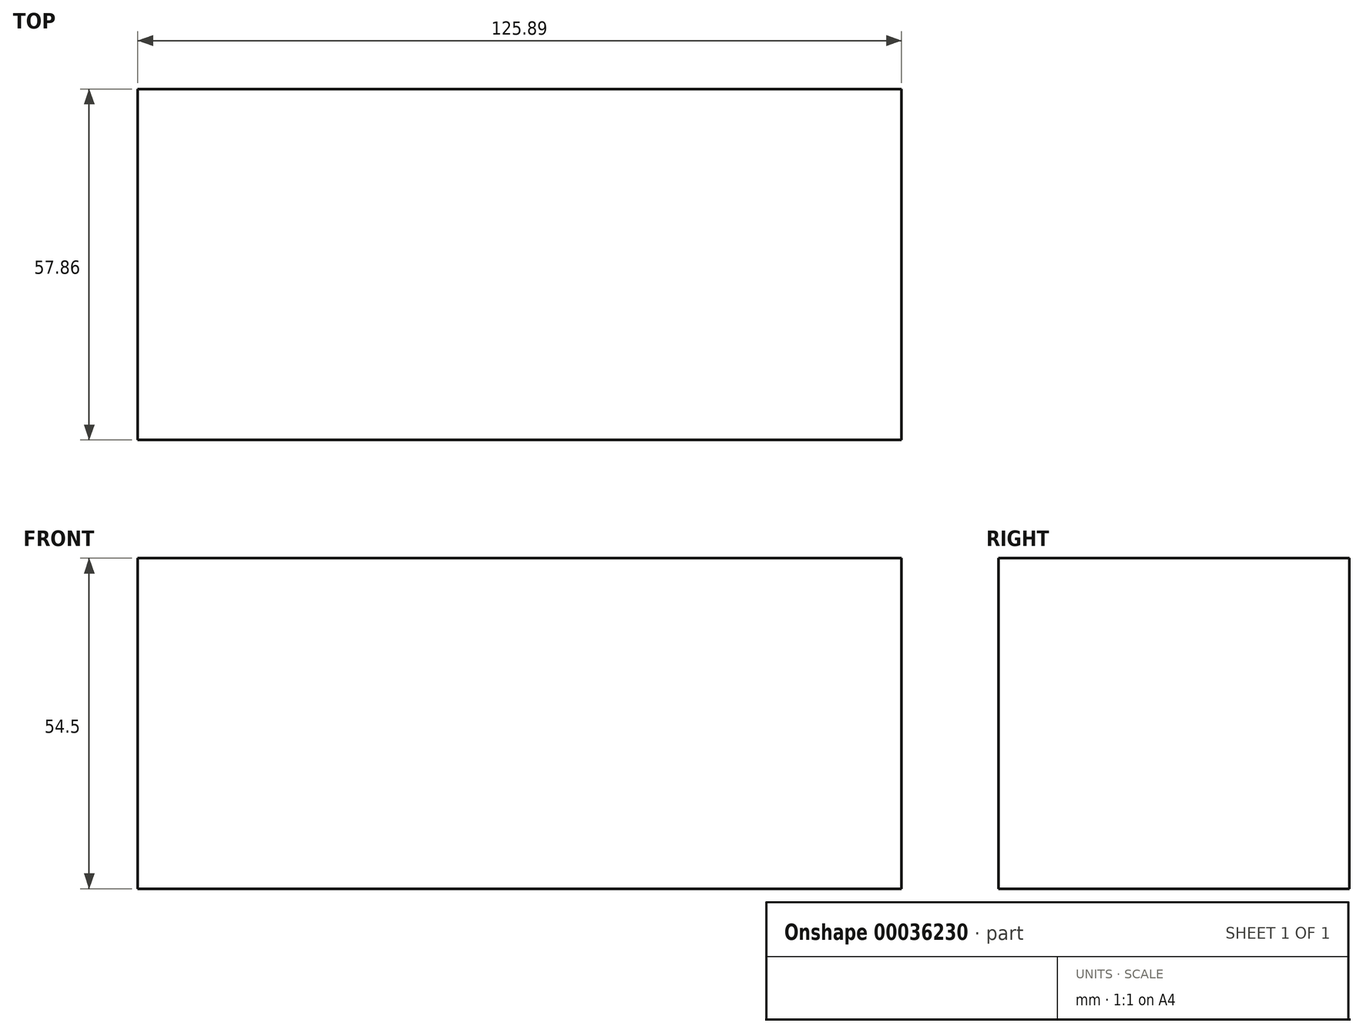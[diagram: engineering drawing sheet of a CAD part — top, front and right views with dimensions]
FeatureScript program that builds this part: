
annotation { "Feature Type Name" : "Feature", "Feature Type Description" : "" }
export const myFeature = defineFeature(function(context is Context, id is Id, definition is map)
    precondition{}
    {
        {
            var Q0;
            Q0=qCreatedBy(makeId("Top.planeOp"),FACE);
            var sketch = newSketch(context, id + "F0", { "sketchPlane" : qUnion([Q0])});
            skLineSegment(sketch, "E0.bottom", {"start": v(-68.17, 29.54) * mm, "end": v(57.72, 29.54) * mm});
            skLineSegment(sketch, "E0.top", {"start": v(-68.17, -28.32) * mm, "end": v(57.72, -28.32) * mm});
            skLineSegment(sketch, "E0.left", {"start": v(-68.17, 29.54) * mm, "end": v(-68.17, -28.32) * mm});
            skLineSegment(sketch, "E0.right", {"start": v(57.72, 29.54) * mm, "end": v(57.72, -28.32) * mm});
            skSolve(sketch);
        }
        {
            var Q0;
            Q0=makeQuery(id+"F0.imprint","IMPRINT",FACE,{"disambiguationData":[TD([[makeQuery(id+"F0.imprint","IMPRINT",EDGE,{"derivedFrom":sQuery(id+"F0.wireOp",EDGE,"E0.bottom")}),-1.0]])]});
            extrude(context, id + "F1", {"entities" : qUnion([Q0]), "depth" : 54.5 * mm, "offsetDistance" : 25 * mm});
        }
    });
